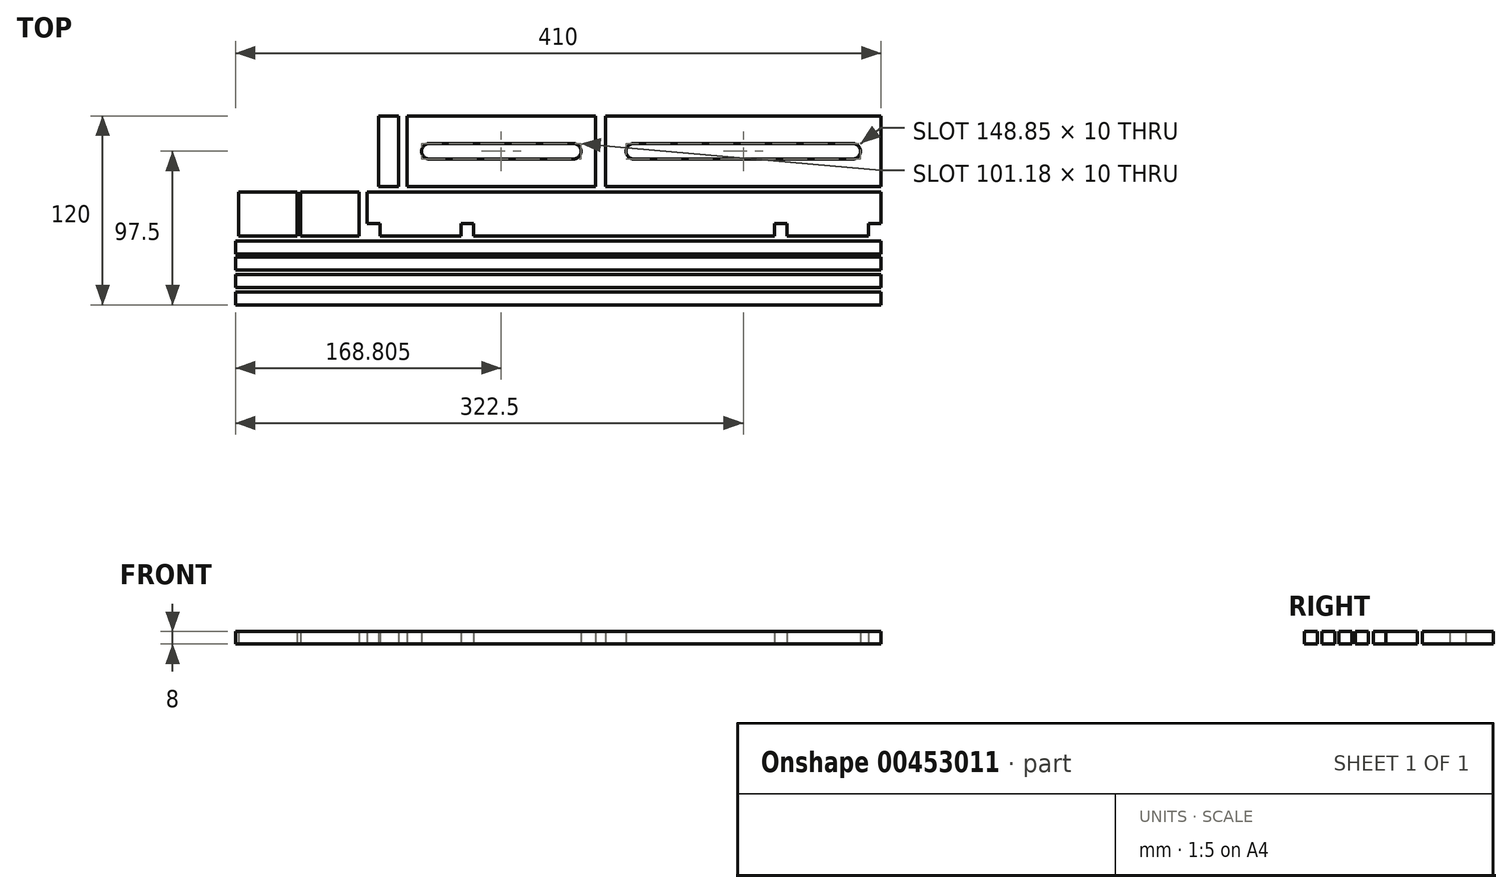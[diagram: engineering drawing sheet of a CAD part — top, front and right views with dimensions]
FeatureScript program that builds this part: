
annotation { "Feature Type Name" : "Feature", "Feature Type Description" : "" }
export const myFeature = defineFeature(function(context is Context, id is Id, definition is map)
    precondition{}
    {
        {
            var Q0;
            Q0=qCreatedBy(makeId("Top.planeOp"),FACE);
            var sketch = newSketch(context, id + "F0", { "sketchPlane" : qUnion([Q0])});
            skLineSegment(sketch, "E0.bottom", {"start": v(205, 60) * mm, "end": v(-205, 60) * mm, "construction": true});
            skLineSegment(sketch, "E0.top", {"start": v(205, -60) * mm, "end": v(-205, -60) * mm, "construction": true});
            skLineSegment(sketch, "E0.left", {"start": v(205, 60) * mm, "end": v(205, -60) * mm, "construction": true});
            skLineSegment(sketch, "E0.right", {"start": v(-205, 60) * mm, "end": v(-205, -60) * mm, "construction": true});
            skPoint(sketch, "E0.middle", {"position": v(0, 0) * mm});
            skLineSegment(sketch, "E1.bottom", {"start": v(205, 60) * mm, "end": v(30, 60) * mm});
            skLineSegment(sketch, "E1.top", {"start": v(205, 15) * mm, "end": v(30, 15) * mm});
            skLineSegment(sketch, "E1.left", {"start": v(205, 60) * mm, "end": v(205, 15) * mm});
            skLineSegment(sketch, "E1.right", {"start": v(30, 60) * mm, "end": v(30, 15) * mm});
            skLineSegment(sketch, "E2.bottom", {"start": v(23.8, 15) * mm, "end": v(-96.2, 15) * mm});
            skLineSegment(sketch, "E2.top", {"start": v(23.8, 60) * mm, "end": v(-96.2, 60) * mm});
            skLineSegment(sketch, "E2.left", {"start": v(23.8, 15) * mm, "end": v(23.8, 60) * mm});
            skLineSegment(sketch, "E2.right", {"start": v(-96.2, 15) * mm, "end": v(-96.2, 60) * mm});
            skLineSegment(sketch, "E3.bottom", {"start": v(-101.4, 15) * mm, "end": v(-114.11, 15) * mm});
            skLineSegment(sketch, "E3.top", {"start": v(-101.4, 60) * mm, "end": v(-114.11, 60) * mm});
            skLineSegment(sketch, "E3.left", {"start": v(-101.4, 15) * mm, "end": v(-101.4, 60) * mm});
            skLineSegment(sketch, "E3.right", {"start": v(-114.11, 15) * mm, "end": v(-114.11, 60) * mm});
            skLineSegment(sketch, "E4", {"start": v(-81.79, 37.5) * mm, "end": v(9.4, 37.5) * mm, "construction": true});
            skPoint(sketch, "E4.startSnap0", {"position": v(-96.2, 37.5) * mm});
            skLineSegment(sketch, "E5", {"start": v(48.08, 37.5) * mm, "end": v(186.92, 37.5) * mm, "construction": true});
            skPoint(sketch, "E5.startSnap0", {"position": v(30, 37.5) * mm});
            skArc(sketch, "E6", {"start": v(-81.79, 42.5) * mm, "mid": v(-86.79, 37.5) * mm, "end": v(-81.79, 32.5) * mm});
            skArc(sketch, "E7", {"start": v(9.4, 32.5) * mm, "mid": v(14.4, 37.5) * mm, "end": v(9.4, 42.5) * mm});
            skArc(sketch, "E8", {"start": v(48.08, 32.5) * mm, "mid": v(43.08, 37.5) * mm, "end": v(48.08, 42.5) * mm});
            skArc(sketch, "E9", {"start": v(186.92, 42.5) * mm, "mid": v(191.92, 37.5) * mm, "end": v(186.92, 32.5) * mm});
            skLineSegment(sketch, "E10", {"start": v(186.92, 32.5) * mm, "end": v(48.08, 32.5) * mm});
            skLineSegment(sketch, "E11", {"start": v(48.08, 42.5) * mm, "end": v(186.92, 42.5) * mm});
            skLineSegment(sketch, "E12", {"start": v(9.4, 42.5) * mm, "end": v(-81.79, 42.5) * mm});
            skLineSegment(sketch, "E13", {"start": v(-81.79, 32.5) * mm, "end": v(9.4, 32.5) * mm});
            skLineSegment(sketch, "E14", {"start": v(-36.2, 60) * mm, "end": v(-36.2, 15) * mm, "construction": true});
            skLineSegment(sketch, "E15", {"start": v(117.5, 60) * mm, "end": v(117.5, 15) * mm, "construction": true});
            skLineSegment(sketch, "E16.bottom", {"start": v(205, 11.75) * mm, "end": v(-121.28, 11.75) * mm});
            skLineSegment(sketch, "E16.left", {"start": v(205, 11.75) * mm, "end": v(205, -8.25) * mm});
            skLineSegment(sketch, "E16.right", {"start": v(-121.28, 11.75) * mm, "end": v(-121.28, -8.25) * mm});
            skLineSegment(sketch, "E17.top", {"start": v(-121.28, -8.25) * mm, "end": v(-113.28, -8.25) * mm});
            skLineSegment(sketch, "E17.right", {"start": v(-113.28, -16.25) * mm, "end": v(-113.28, -8.25) * mm});
            skLineSegment(sketch, "E18.bottom", {"start": v(-61.69, -8.25) * mm, "end": v(-53.69, -8.25) * mm});
            skLineSegment(sketch, "E18.left", {"start": v(-61.69, -8.25) * mm, "end": v(-61.69, -16.25) * mm});
            skLineSegment(sketch, "E18.right", {"start": v(-53.69, -8.25) * mm, "end": v(-53.69, -16.25) * mm});
            skLineSegment(sketch, "E19.bottom", {"start": v(137.41, -8.25) * mm, "end": v(145.41, -8.25) * mm});
            skLineSegment(sketch, "E19.left", {"start": v(137.41, -8.25) * mm, "end": v(137.41, -16.25) * mm});
            skLineSegment(sketch, "E19.right", {"start": v(145.41, -8.25) * mm, "end": v(145.41, -16.25) * mm});
            skLineSegment(sketch, "E20.trimOffspring", {"start": v(-61.69, -16.25) * mm, "end": v(-113.28, -16.25) * mm});
            skLineSegment(sketch, "E21.trimOffspring", {"start": v(137.41, -16.25) * mm, "end": v(-53.69, -16.25) * mm});
            skLineSegment(sketch, "E22.trimOffspring", {"start": v(197, -16.25) * mm, "end": v(145.41, -16.25) * mm});
            skLineSegment(sketch, "E23.top", {"start": v(205, -8.25) * mm, "end": v(197, -8.25) * mm});
            skLineSegment(sketch, "E23.right", {"start": v(197, -16.25) * mm, "end": v(197, -8.25) * mm});
            skLineSegment(sketch, "E24.bottom", {"start": v(205, -19.5) * mm, "end": v(-205, -19.5) * mm});
            skLineSegment(sketch, "E24.top", {"start": v(205, -27.65) * mm, "end": v(-205, -27.65) * mm});
            skLineSegment(sketch, "E24.left", {"start": v(205, -19.5) * mm, "end": v(205, -27.65) * mm});
            skLineSegment(sketch, "E24.right", {"start": v(-205, -19.5) * mm, "end": v(-205, -27.65) * mm});
            skLineSegment(sketch, "E25.bottom", {"start": v(205, -29.83) * mm, "end": v(-205, -29.83) * mm});
            skLineSegment(sketch, "E25.top", {"start": v(205, -37.98) * mm, "end": v(-205, -37.98) * mm});
            skLineSegment(sketch, "E25.left", {"start": v(205, -29.83) * mm, "end": v(205, -37.98) * mm});
            skLineSegment(sketch, "E25.right", {"start": v(-205, -29.83) * mm, "end": v(-205, -37.98) * mm});
            skLineSegment(sketch, "E26.bottom", {"start": v(205, -60) * mm, "end": v(-205, -60) * mm});
            skLineSegment(sketch, "E26.top", {"start": v(205, -51.85) * mm, "end": v(-205, -51.85) * mm});
            skLineSegment(sketch, "E26.left", {"start": v(205, -60) * mm, "end": v(205, -51.85) * mm});
            skLineSegment(sketch, "E26.right", {"start": v(-205, -60) * mm, "end": v(-205, -51.85) * mm});
            skLineSegment(sketch, "E27.bottom", {"start": v(205, -40.8) * mm, "end": v(-205, -40.8) * mm});
            skLineSegment(sketch, "E27.top", {"start": v(205, -48.94) * mm, "end": v(-205, -48.94) * mm});
            skLineSegment(sketch, "E27.left", {"start": v(205, -40.8) * mm, "end": v(205, -48.94) * mm});
            skLineSegment(sketch, "E27.right", {"start": v(-205, -40.8) * mm, "end": v(-205, -48.94) * mm});
            skLineSegment(sketch, "E28.bottom", {"start": v(-126.57, 11.75) * mm, "end": v(-163.6, 11.75) * mm});
            skLineSegment(sketch, "E28.top", {"start": v(-126.57, -16.25) * mm, "end": v(-163.6, -16.25) * mm});
            skLineSegment(sketch, "E28.left", {"start": v(-126.57, 11.75) * mm, "end": v(-126.57, -16.25) * mm});
            skLineSegment(sketch, "E28.right", {"start": v(-163.6, 11.75) * mm, "end": v(-163.6, -16.25) * mm});
            skLineSegment(sketch, "E29.bottom", {"start": v(-165.98, 11.75) * mm, "end": v(-203.01, 11.75) * mm});
            skLineSegment(sketch, "E29.top", {"start": v(-165.98, -16.25) * mm, "end": v(-203.01, -16.25) * mm});
            skLineSegment(sketch, "E29.left", {"start": v(-165.98, 11.75) * mm, "end": v(-165.98, -16.25) * mm});
            skLineSegment(sketch, "E29.right", {"start": v(-203.01, 11.75) * mm, "end": v(-203.01, -16.25) * mm});
            skLineSegment(sketch, "E30", {"start": v(41.86, 11.75) * mm, "end": v(41.86, -16.25) * mm, "construction": true});
            skPoint(sketch, "E31", {"position": v(41.86, 5.64) * mm});
            skPoint(sketch, "E32", {"position": v(-110.09, 5.64) * mm});
            skPoint(sketch, "E33", {"position": v(193.8, 5.64) * mm});
            skSolve(sketch);
        }
        {
            var Q0;
            Q0 = qSketchRegion(id + "F0", true);
            extrude(context, id + "F1", {"entities" : qUnion([Q0]), "depth" : 8 * mm});
        }
    });
